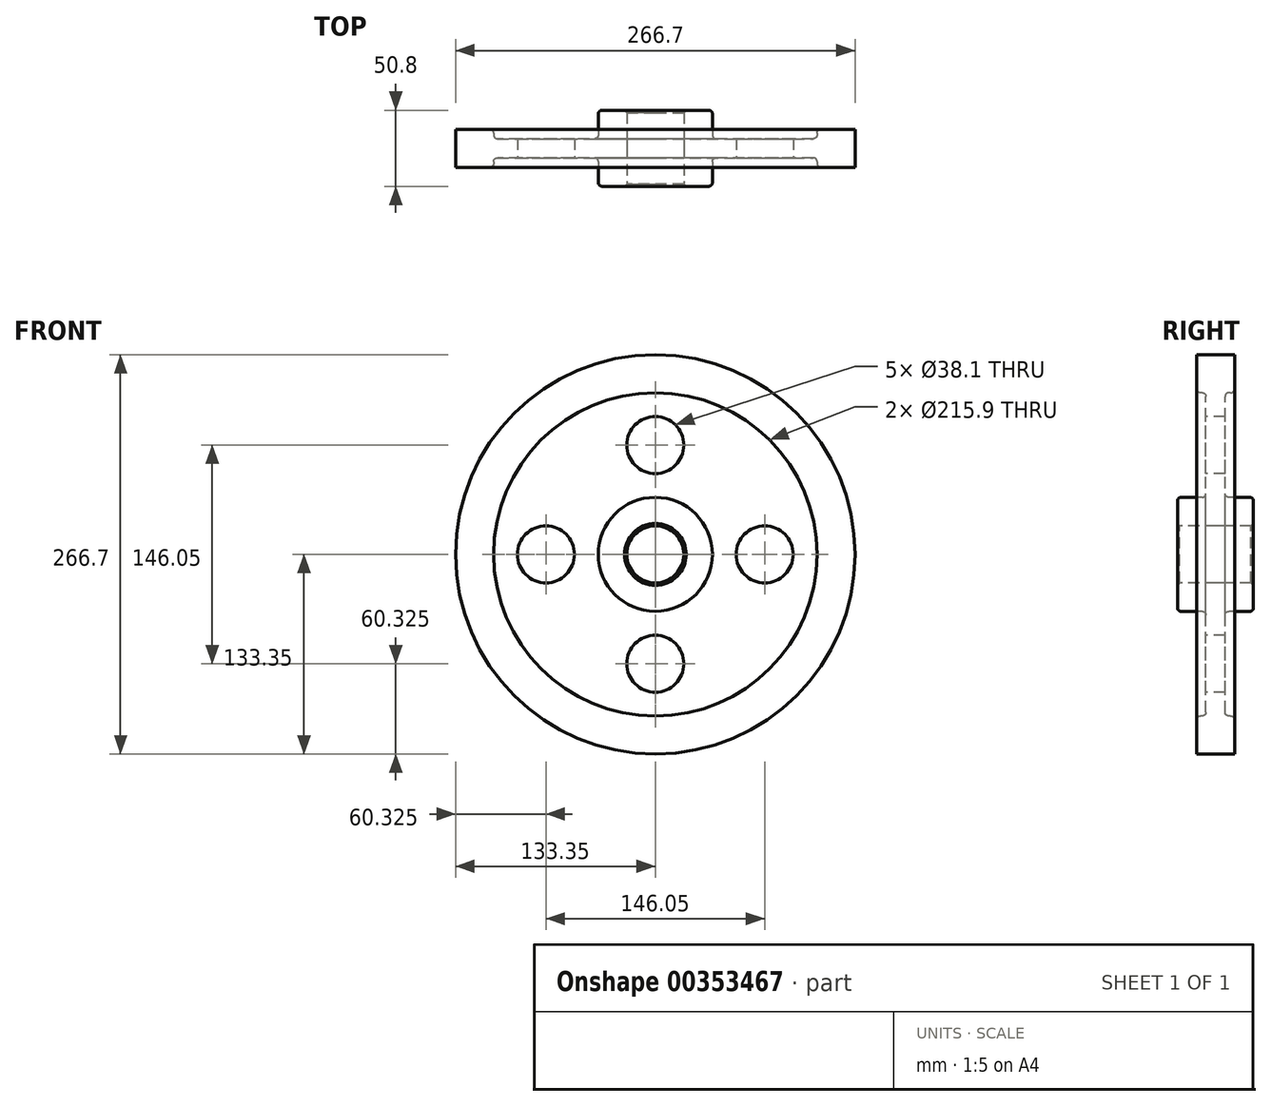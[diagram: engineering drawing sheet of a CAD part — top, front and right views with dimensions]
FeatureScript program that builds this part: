
annotation { "Feature Type Name" : "Feature", "Feature Type Description" : "" }
export const myFeature = defineFeature(function(context is Context, id is Id, definition is map)
    precondition{}
    {
        {
            var Q0;
            Q0=qCreatedBy(makeId("Right.planeOp"),FACE);
            var sketch = newSketch(context, id + "F0", { "sketchPlane" : qUnion([Q0])});
            skLineSegment(sketch, "E0", {"start": v(0, 0) * mm, "end": v(75.9, 0) * mm, "construction": true});
            skLineSegment(sketch, "E1.0", {"start": v(0, 19.05) * mm, "end": v(25.4, 19.05) * mm});
            skLineSegment(sketch, "E2.0", {"start": v(6.35, 38.1) * mm, "end": v(25.4, 38.1) * mm});
            skLineSegment(sketch, "E3.0", {"start": v(6.35, 107.95) * mm, "end": v(12.7, 107.95) * mm});
            skLineSegment(sketch, "E4.0", {"start": v(0, 133.35) * mm, "end": v(12.7, 133.35) * mm});
            skLineSegment(sketch, "E5", {"start": v(0, 0) * mm, "end": v(0, 133.35) * mm, "construction": true});
            skLineSegment(sketch, "E6.0", {"start": v(25.4, 19.05) * mm, "end": v(25.4, 38.1) * mm});
            skLineSegment(sketch, "E7.0", {"start": v(6.35, 38.1) * mm, "end": v(6.35, 107.95) * mm});
            skLineSegment(sketch, "E8.trimOffspring", {"start": v(12.7, 107.95) * mm, "end": v(12.7, 133.35) * mm});
            skLineSegment(sketch, "E9.MirrorCS", {"start": v(0, 133.35) * mm, "end": v(-12.7, 133.35) * mm});
            skLineSegment(sketch, "E10.MirrorCS", {"start": v(-12.7, 107.95) * mm, "end": v(-12.7, 133.35) * mm});
            skLineSegment(sketch, "E11.MirrorCS", {"start": v(-6.35, 107.95) * mm, "end": v(-12.7, 107.95) * mm});
            skLineSegment(sketch, "E12.MirrorCS", {"start": v(-6.35, 38.1) * mm, "end": v(-6.35, 107.95) * mm});
            skLineSegment(sketch, "E13.MirrorCS", {"start": v(-6.35, 38.1) * mm, "end": v(-25.4, 38.1) * mm});
            skLineSegment(sketch, "E14.MirrorCS", {"start": v(-25.4, 19.05) * mm, "end": v(-25.4, 38.1) * mm});
            skLineSegment(sketch, "E15.MirrorCS", {"start": v(0, 19.05) * mm, "end": v(-25.4, 19.05) * mm});
            skSolve(sketch);
        }
        {
            var Q0;
            Q0=makeQuery(id+"F0.imprint","IMPRINT",FACE,{"disambiguationData":[TD([[makeQuery(id+"F0.imprint","IMPRINT",EDGE,{"derivedFrom":sQuery(id+"F0.wireOp",EDGE,"E1.0")}),1.0]])]});
            var Q1;
            Q1=sQuery(id+"F0.wireOp",EDGE,"E0");
            revolve(context, id + "F1", {"entities" : qUnion([Q0]), "axis" : qUnion([Q1]), "revolveType" : RevolveType.FULL});
        }
        {
            var Q0;
            Q0=makeQuery(id+"F1.opRevolve","SWEPT_FACE",FACE,{"disambiguationData":[OSD([sQuery(id+"F0.wireOp",EDGE,"E12.MirrorCS")])]});
            var sketch = newSketch(context, id + "F2", { "sketchPlane" : qUnion([Q0])});
            skLineSegment(sketch, "E16", {"start": v(0, 0) * mm, "end": v(0, 73.03) * mm});
            skCircle(sketch, "E17", {"center": v(0, 73.03) * mm, "radius": 19.05 * mm});
            skCircle(sketch, "E18.1.0", {"center": v(-73.03, 0) * mm, "radius": 19.05 * mm});
            skCircle(sketch, "E18.2.0", {"center": v(0, -73.03) * mm, "radius": 19.05 * mm});
            skCircle(sketch, "E18.3.0", {"center": v(73.03, 0) * mm, "radius": 19.05 * mm});
            skPoint(sketch, "E18.center", {"position": v(0, 0) * mm});
            skSolve(sketch);
        }
        {
            var Q0;
            Q0=makeQuery(id+"F2.imprint","IMPRINT",FACE,{"disambiguationData":[TD([[makeQuery(id+"F2.imprint","IMPRINT",EDGE,{"derivedFrom":sQuery(id+"F2.wireOp",EDGE,"E18.3.0")}),1.0]])]});
            var Q1;
            Q1=makeQuery(id+"F2.imprint","IMPRINT",FACE,{"disambiguationData":[TD([[makeQuery(id+"F2.imprint","IMPRINT",EDGE,{"derivedFrom":sQuery(id+"F2.wireOp",EDGE,"E18.2.0")}),1.0]])]});
            var Q2;
            Q2=makeQuery(id+"F2.imprint","IMPRINT",FACE,{"disambiguationData":[TD([[makeQuery(id+"F2.imprint","IMPRINT",EDGE,{"derivedFrom":sQuery(id+"F2.wireOp",EDGE,"E18.1.0")}),1.0]])]});
            var Q3;
            Q3=makeQuery(id+"F2.imprint","IMPRINT",FACE,{"disambiguationData":[TD([[makeQuery(id+"F2.imprint","IMPRINT",EDGE,{"derivedFrom":sQuery(id+"F2.wireOp",EDGE,"E17")}),1.0]])]});
            extrude(context, id + "F3", {"entities" : qUnion([Q0, Q1, Q2, Q3]), "operationType" : NewBodyOperationType.REMOVE, "oppositeDirection" : true, "depth" : 25.4 * mm});
        }
        {
            var Q0;
            Q0=makeQuery(id+"F1.opRevolve","SWEPT_EDGE",EDGE,{"disambiguationData":[OSD([sQuery(id+"F0.wireOp",EDGE,"E12.MirrorCS"),sQuery(id+"F0.wireOp",EDGE,"E13.MirrorCS")])]});
            var Q1;
            Q1=makeQuery(id+"F1.opRevolve","SWEPT_EDGE",EDGE,{"disambiguationData":[OSD([sQuery(id+"F0.wireOp",EDGE,"E13.MirrorCS"),sQuery(id+"F0.wireOp",EDGE,"E14.MirrorCS")])]});
            var Q2;
            Q2=makeQuery(id+"F1.opRevolve","SWEPT_EDGE",EDGE,{"disambiguationData":[OSD([sQuery(id+"F0.wireOp",EDGE,"E10.MirrorCS"),sQuery(id+"F0.wireOp",EDGE,"E11.MirrorCS")])]});
            var Q3;
            Q3=makeQuery(id+"F1.opRevolve","SWEPT_EDGE",EDGE,{"disambiguationData":[OSD([sQuery(id+"F0.wireOp",EDGE,"E11.MirrorCS"),sQuery(id+"F0.wireOp",EDGE,"E12.MirrorCS")])]});
            fillet(context, id + "F4", {"entities" : qUnion([Q0, Q1, Q2, Q3]), "radius" : 2.54 * mm, "tangentPropagation" : true, "allowEdgeOverflow" : false});
        }
        {
            var Q0;
            Q0=makeQuery(id+"F1.opRevolve","SWEPT_EDGE",EDGE,{"disambiguationData":[OSD([sQuery(id+"F0.wireOp",EDGE,"E14.MirrorCS"),sQuery(id+"F0.wireOp",EDGE,"E15.MirrorCS")])]});
            var Q1;
            Q1=makeQuery(id+"F1.opRevolve","SWEPT_EDGE",EDGE,{"disambiguationData":[OSD([sQuery(id+"F0.wireOp",EDGE,"E1.0"),sQuery(id+"F0.wireOp",EDGE,"E6.0")])]});
            chamfer(context, id + "F5", {"entities" : qUnion([Q0, Q1]), "width" : 1.59 * mm, "tangentPropagation" : true});
        }
        {
            var Q0;
            Q0=makeQuery(id+"F1.opRevolve","SWEPT_EDGE",EDGE,{"disambiguationData":[OSD([sQuery(id+"F0.wireOp",EDGE,"E2.0"),sQuery(id+"F0.wireOp",EDGE,"E6.0")])]});
            var Q1;
            Q1=makeQuery(id+"F1.opRevolve","SWEPT_EDGE",EDGE,{"disambiguationData":[OSD([sQuery(id+"F0.wireOp",EDGE,"E2.0"),sQuery(id+"F0.wireOp",EDGE,"E7.0")])]});
            var Q2;
            Q2=makeQuery(id+"F1.opRevolve","SWEPT_EDGE",EDGE,{"disambiguationData":[OSD([sQuery(id+"F0.wireOp",EDGE,"E3.0"),sQuery(id+"F0.wireOp",EDGE,"E8.trimOffspring")])]});
            var Q3;
            Q3=makeQuery(id+"F1.opRevolve","SWEPT_EDGE",EDGE,{"disambiguationData":[OSD([sQuery(id+"F0.wireOp",EDGE,"E3.0"),sQuery(id+"F0.wireOp",EDGE,"E7.0")])]});
            fillet(context, id + "F6", {"entities" : qUnion([Q0, Q1, Q2, Q3]), "radius" : 2.54 * mm, "tangentPropagation" : true, "allowEdgeOverflow" : false});
        }
    });
